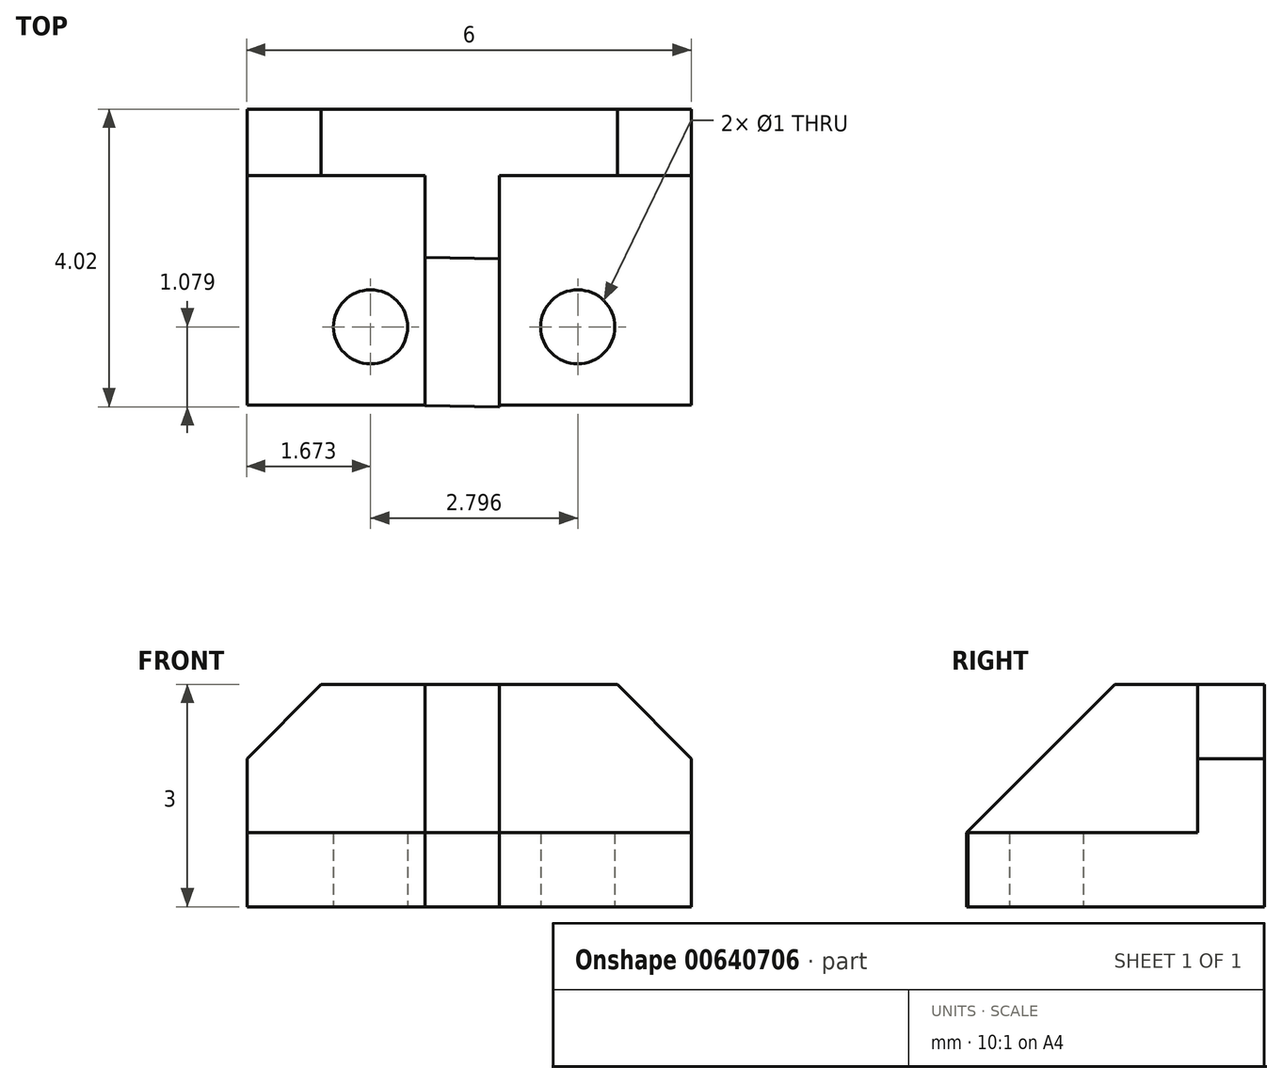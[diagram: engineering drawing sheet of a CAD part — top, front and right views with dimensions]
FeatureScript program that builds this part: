
annotation { "Feature Type Name" : "Feature", "Feature Type Description" : "" }
export const myFeature = defineFeature(function(context is Context, id is Id, definition is map)
    precondition{}
    {
        {
            var Q0;
            Q0=qCreatedBy(makeId("Top.planeOp"),FACE);
            var sketch = newSketch(context, id + "F0", { "sketchPlane" : qUnion([Q0])});
            skLineSegment(sketch, "E0", {"start": v(-3.2, 0) * mm, "end": v(2.8, 0) * mm});
            skLineSegment(sketch, "E1", {"start": v(2.8, 0) * mm, "end": v(2.8, 4) * mm});
            skLineSegment(sketch, "E2", {"start": v(2.8, 4) * mm, "end": v(-3.2, 4) * mm});
            skLineSegment(sketch, "E3", {"start": v(-3.2, 4) * mm, "end": v(-3.2, 0) * mm});
            skCircle(sketch, "E4", {"center": v(-1.53, 1.06) * mm, "radius": 0.5 * mm});
            skCircle(sketch, "E5", {"center": v(1.27, 1.06) * mm, "radius": 0.5 * mm});
            skLineSegment(sketch, "E6", {"start": v(-3.2, 3.1) * mm, "end": v(2.8, 3.1) * mm});
            skSolve(sketch);
        }
        {
            var Q0;
            Q0=makeQuery(id+"F0.imprint","IMPRINT",FACE,{"disambiguationData":[TD([[makeQuery(id+"F0.imprint","IMPRINT",EDGE,{"derivedFrom":sQuery(id+"F0.wireOp",EDGE,"E0")}),1.0]])]});
            extrude(context, id + "F1", {"entities" : qUnion([Q0]), "depth" : 1 * mm, "offsetDistance" : 25 * mm});
        }
        {
            var Q0;
            {var subQ0=sQuery(id+"F0.wireOp",EDGE,"E2");Q0=makeQuery(id+"F0.imprint","IMPRINT",FACE,{"disambiguationData":[TD([[makeQuery(id+"F0.imprint","IMPRINT",EDGE,{"derivedFrom":subQ0}),1.0]])]});}
            extrude(context, id + "F2", {"entities" : qUnion([Q0]), "operationType" : NewBodyOperationType.ADD, "depth" : 3 * mm, "offsetDistance" : 25 * mm});
        }
        {
            var Q0;
            Q0=qCreatedBy(makeId("Top.planeOp"),FACE);
            var sketch = newSketch(context, id + "F3", { "sketchPlane" : qUnion([Q0])});
            skLineSegment(sketch, "E7", {"start": v(-0.8, 3.17) * mm, "end": v(-0.8, 0) * mm});
            skLineSegment(sketch, "E8", {"start": v(0.2, 3.16) * mm, "end": v(0.2, -0.02) * mm});
            skLineSegment(sketch, "E9", {"start": v(0.2, 3.16) * mm, "end": v(-0.8, 3.17) * mm});
            skLineSegment(sketch, "E10", {"start": v(0.2, -0.02) * mm, "end": v(-0.8, 0) * mm});
            skSolve(sketch);
        }
        {
            var Q0;
            Q0=makeQuery(id+"F3.imprint","IMPRINT",FACE,{"disambiguationData":[TD([[makeQuery(id+"F3.imprint","IMPRINT",EDGE,{"derivedFrom":sQuery(id+"F3.wireOp",EDGE,"E7")}),1.0]])]});
            extrude(context, id + "F4", {"entities" : qUnion([Q0]), "operationType" : NewBodyOperationType.ADD, "depth" : 3 * mm, "offsetDistance" : 25 * mm});
        }
        {
            var Q0;
            Q0=makeQuery(id+"F2.opExtrude","CAP_EDGE",EDGE,{"disambiguationData":[OSD([sQuery(id+"F0.wireOp",EDGE,"E1")])],"isStart":false});
            chamfer(context, id + "F5", {"entities" : qUnion([Q0]), "width" : 1 * mm, "tangentPropagation" : true});
        }
        {
            var Q0;
            Q0=makeQuery(id+"F2.opExtrude","CAP_EDGE",EDGE,{"disambiguationData":[OSD([sQuery(id+"F0.wireOp",EDGE,"E3")])],"isStart":false});
            chamfer(context, id + "F6", {"entities" : qUnion([Q0]), "width" : 1 * mm, "tangentPropagation" : true});
        }
        {
            var Q0;
            Q0=makeQuery(id+"F4.opExtrude","CAP_EDGE",EDGE,{"disambiguationData":[OSD([sQuery(id+"F3.wireOp",EDGE,"E10")])],"isStart":false});
            chamfer(context, id + "F7", {"entities" : qUnion([Q0]), "width" : 2 * mm, "tangentPropagation" : true});
        }
    });
